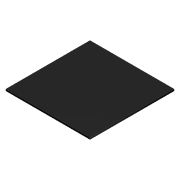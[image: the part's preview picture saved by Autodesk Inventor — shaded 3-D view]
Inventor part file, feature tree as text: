
AUTODESK INVENTOR PART (.ipt)
format: ipt  version: 2012 (Build 160160000, 160)  size: 71,168 bytes
history: native  units: in
note: dims shown in document units (in); Inventor stores cm internally (conversion verified against a paired STEP export)
features: extrude x1, sketch x1
ambient origin geometry x8: Origin, YZ Plane, XZ Plane, XY Plane, X Axis, Y Axis, Z Axis, Center Point
bodies: Solid1 (feature_tree)
feature tree (2):
  extrude  "Extrusion1"  Depth=6.0in
  sketch  "Sketch1"  dims[d0=0.125in d1=6.0in d2=6.0in d3=0.0in]
